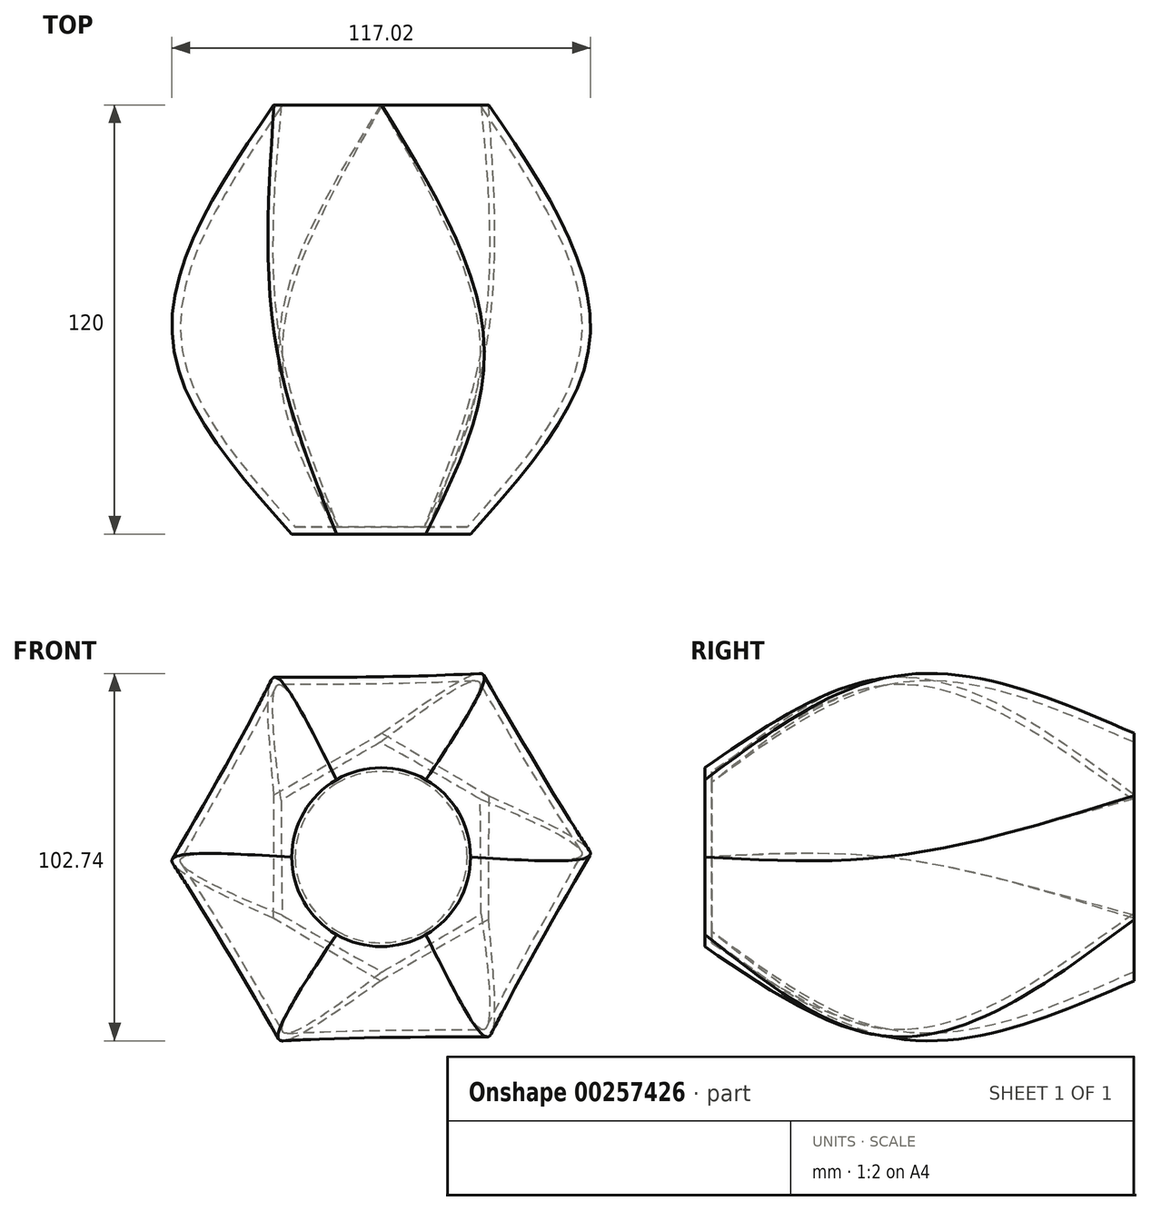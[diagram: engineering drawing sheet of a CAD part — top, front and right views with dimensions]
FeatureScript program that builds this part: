
annotation { "Feature Type Name" : "Feature", "Feature Type Description" : "" }
export const myFeature = defineFeature(function(context is Context, id is Id, definition is map)
    precondition{}
    {
        {
            var Q0;
            Q0=qCreatedBy(makeId("Front.planeOp"),FACE);
            var sketch = newSketch(context, id + "F0", { "sketchPlane" : qUnion([Q0])});
            skCircle(sketch, "E0.cCircle", {"center": v(0, 0) * mm, "radius": 30 * mm, "construction": true});
            skLineSegment(sketch, "E0.0", {"start": v(-29.92, 17.45) * mm, "end": v(0.15, 34.64) * mm});
            skLineSegment(sketch, "E0.1", {"start": v(0.15, 34.64) * mm, "end": v(30.08, 17.19) * mm});
            skLineSegment(sketch, "E0.2", {"start": v(30.08, 17.19) * mm, "end": v(29.92, -17.45) * mm});
            skLineSegment(sketch, "E0.3", {"start": v(29.92, -17.45) * mm, "end": v(-0.15, -34.64) * mm});
            skLineSegment(sketch, "E0.4", {"start": v(-0.15, -34.64) * mm, "end": v(-30.08, -17.19) * mm});
            skLineSegment(sketch, "E0.5", {"start": v(-30.08, -17.19) * mm, "end": v(-29.92, 17.45) * mm});
            skPoint(sketch, "E0.0.midPoint", {"position": v(-14.88, 26.05) * mm});
            skSolve(sketch);
        }
        {
            var Q0;
            Q0=qCreatedBy(makeId("Front.planeOp"),FACE);
            cPlane(context, id + "F1", {"entities" : qUnion([Q0]), "cplaneType" : CPlaneType.OFFSET, "offset" : 70 * mm, "width" : 150 * mm, "height" : 150 * mm});
        }
        {
            var Q0;
            Q0=qCreatedBy(id+"F1.planeOp",FACE);
            var sketch = newSketch(context, id + "F2", { "sketchPlane" : qUnion([Q0])});
            skCircle(sketch, "E1.cCircle", {"center": v(0, 0) * mm, "radius": 50 * mm, "construction": true});
            skLineSegment(sketch, "E1.0", {"start": v(-28.87, 50) * mm, "end": v(28.87, 50) * mm});
            skLineSegment(sketch, "E1.1", {"start": v(28.87, 50) * mm, "end": v(57.74, 0) * mm});
            skLineSegment(sketch, "E1.2", {"start": v(57.74, 0) * mm, "end": v(28.87, -50) * mm});
            skLineSegment(sketch, "E1.3", {"start": v(28.87, -50) * mm, "end": v(-28.87, -50) * mm});
            skLineSegment(sketch, "E1.4", {"start": v(-28.87, -50) * mm, "end": v(-57.74, 0) * mm});
            skLineSegment(sketch, "E1.5", {"start": v(-57.74, 0) * mm, "end": v(-28.87, 50) * mm});
            skPoint(sketch, "E1.0.midPoint", {"position": v(0, 50) * mm});
            skSolve(sketch);
        }
        {
            var Q0;
            Q0=qCreatedBy(id+"F1.planeOp",FACE);
            cPlane(context, id + "F3", {"entities" : qUnion([Q0]), "cplaneType" : CPlaneType.OFFSET, "offset" : 50 * mm, "width" : 150 * mm, "height" : 150 * mm});
        }
        {
            var Q0;
            Q0=qCreatedBy(id+"F3.planeOp",FACE);
            var sketch = newSketch(context, id + "F4", { "sketchPlane" : qUnion([Q0])});
            skCircle(sketch, "E2", {"center": v(0, 0) * mm, "radius": 25 * mm});
            skSolve(sketch);
        }
        {
            var Q0;
            Q0=makeQuery(id+"F0.imprint","IMPRINT",FACE,{"disambiguationData":[TD([[makeQuery(id+"F0.imprint","IMPRINT",EDGE,{"derivedFrom":sQuery(id+"F0.wireOp",EDGE,"E0.0")}),-1.0]])]});
            var Q1;
            Q1=makeQuery(id+"F2.imprint","IMPRINT",FACE,{"disambiguationData":[TD([[makeQuery(id+"F2.imprint","IMPRINT",EDGE,{"derivedFrom":sQuery(id+"F2.wireOp",EDGE,"E1.0")}),-1.0]])]});
            var Q2;
            Q2=makeQuery(id+"F4.imprint","IMPRINT",FACE,{"disambiguationData":[TD([[makeQuery(id+"F4.imprint","IMPRINT",EDGE,{"derivedFrom":sQuery(id+"F4.wireOp",EDGE,"E2")}),1.0]])]});
            loft(context, id + "F5", {"sheetProfilesArray" : [{ "sheetProfileEntities" : qUnion([Q0]) }, { "sheetProfileEntities" : qUnion([Q1]) }, { "sheetProfileEntities" : qUnion([Q2]) }]});
        }
        {
            var Q0;
            Q0=makeQuery(id+"F5.opLoft","CAP_FACE",FACE,{"disambiguationData":[OSD([makeQuery(id+"F0.imprint","IMPRINT",FACE,{"disambiguationData":[TD([[makeQuery(id+"F0.imprint","IMPRINT",EDGE,{"derivedFrom":sQuery(id+"F0.wireOp",EDGE,"E0.0")}),-1.0]])]})])],"isStart":true});
            shell(context, id + "F6", {"entities" : qUnion([Q0]), "thickness" : 2 * mm});
        }
    });
